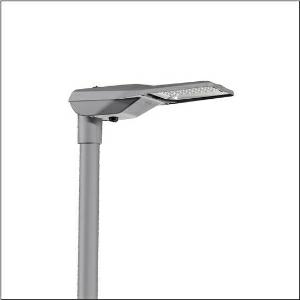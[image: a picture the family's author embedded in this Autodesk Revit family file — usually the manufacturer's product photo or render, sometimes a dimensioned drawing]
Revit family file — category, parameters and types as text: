
# Revit family: streetlight_sl_21_iq_mini___p0_8a_5xe2u31y08jb_ffd0
name_source: partatom
category: Lighting Fixtures
units: mm (PartAtom-declared; Revit-internal decimal feet)

## family parameters
Cut with Voids When Loaded = No
Host = Face
Light Source = No
Part Type = Normal
Room Calculation Point = No
Round Connector Dimension = Use Diameter
Shared = No

## types (1)
- --- (1 x LED, 11310 lm, 72.5 W, 3000K)
    Apparent Load = 73 VA
    CIE Flux Codes = 36 69 97 100 100
    Color Rendering = 70
    Color Temperature = 3000K
    Default Elevation = 1800 mm
    Description = Streetlight SL 21 iQ mini, mast luminaire, primary light control with lens, of PMMA, primary optical cover: cover, of toughened safety glass, transparent, light distribution: P0.8a, light emission: direct distribution, primary light characteristic: asymmetric, installation type: post-top, side-entry, LED, High Power LED, rated luminous flux: 11.310lm, luminous efficacy: 156lm/W, light colour: 730, colour temperature: 3000K, control gear: iQ-Street Remote, D4i with power reduction, control: pre-setting: logarithmic dimming characteristic, Street-Remote, Auto-Match, Temp-Guard, Lumen-Switch, Night-Set, Smart-Wire, Light-Fading, Desk-Remote (wireless, voltage-free reading and setting of iQ features in the workshop via application-optimized NFC function/RFID function), optimised constant luminous flux control (CLO 2.0), mains connection: 220..240V, AC, 50/60Hz, start of lifetime: 73W, end of service life: 76W, reduction: 33W, luminaire housing, of diecast aluminium, powder-coated, Siteco® metallic grey (DB 702S), corrosivity category C5 mid according to DIN EN ISO 12944, please order mast flange separately, inclination adjustable: 0°, 5°, 10°, 15°, sealing non-destructively replaceable, multi-level sealing system, length: 628mm, width: 235mm, height: 110mm, mast flange for spigot size: 42mm (side-entry): 5XC10008XM4, 60/48mm (side-entry/post-top): 5XC10108XM2, 76/60mm (side-entry/post-top): 5XC10108XM1, mounting height: 4..8m, Smart Interface below and above, protection rating (complete): IP66, insulation class (complete): insulation class II (safety insulation), certification: CE, ENEC, ENEC+, VDE, impact resistance: IK09, permissible operating ambient temperature for outdoor applications: -40..+50°C, standard-compliant lighting for roads and squares, packaging unit: 1 piece

Light Distribution: P0.8a
    Height = 110 mm
    Lamp = 1 x LED
    Lamp Light Flux = 11310 lm
    Lamp Power = 72.5 W
    Lamp count = 1
    Length = 625 mm
    Luminous efficacy = 156 lm/W
    Manufacturer = Siteco
    ModVariant = No
    Model = 5XE2U31Y08JB
    Number of Poles = 1
    OnlyDefault = Yes
    Power Factor = 1
    Product Name = Streetlight SL 21 iQ mini | P0.8a
    Product group = mast luminaire | pylon top
    ProductGroupID = 6100
    Protection Class = Protection class II
    Protection Degree = IP 66
    RLX_Detail_Level = 1
    RLX_Emergency_Light_Flux = 0 lm
    RLX_Emergency_Type = 0
    RLX_Emergency_Type_DB = No
    RlxData = <blob elided: 92633 chars, md5=48fbc90e>
    Socket = socket
    Standby Power = 0 W
    System Light Flux = 11310 lm
    System Power = 73 W
    Type Comments = factory setting: luminous flux: 100 % | dim-lin: 254 | 755 mA
    Type Image = l_1003514.jpg
    URL = http://relux.com
    VarID = @adj_069066
    Voltage = 0 V
    Weight = 0.00 kg
    Width = 234 mm

## geometry (parser evidence)
native form markers: Blend x4, Sweep x12
no freeform markers — native parametric forms only
